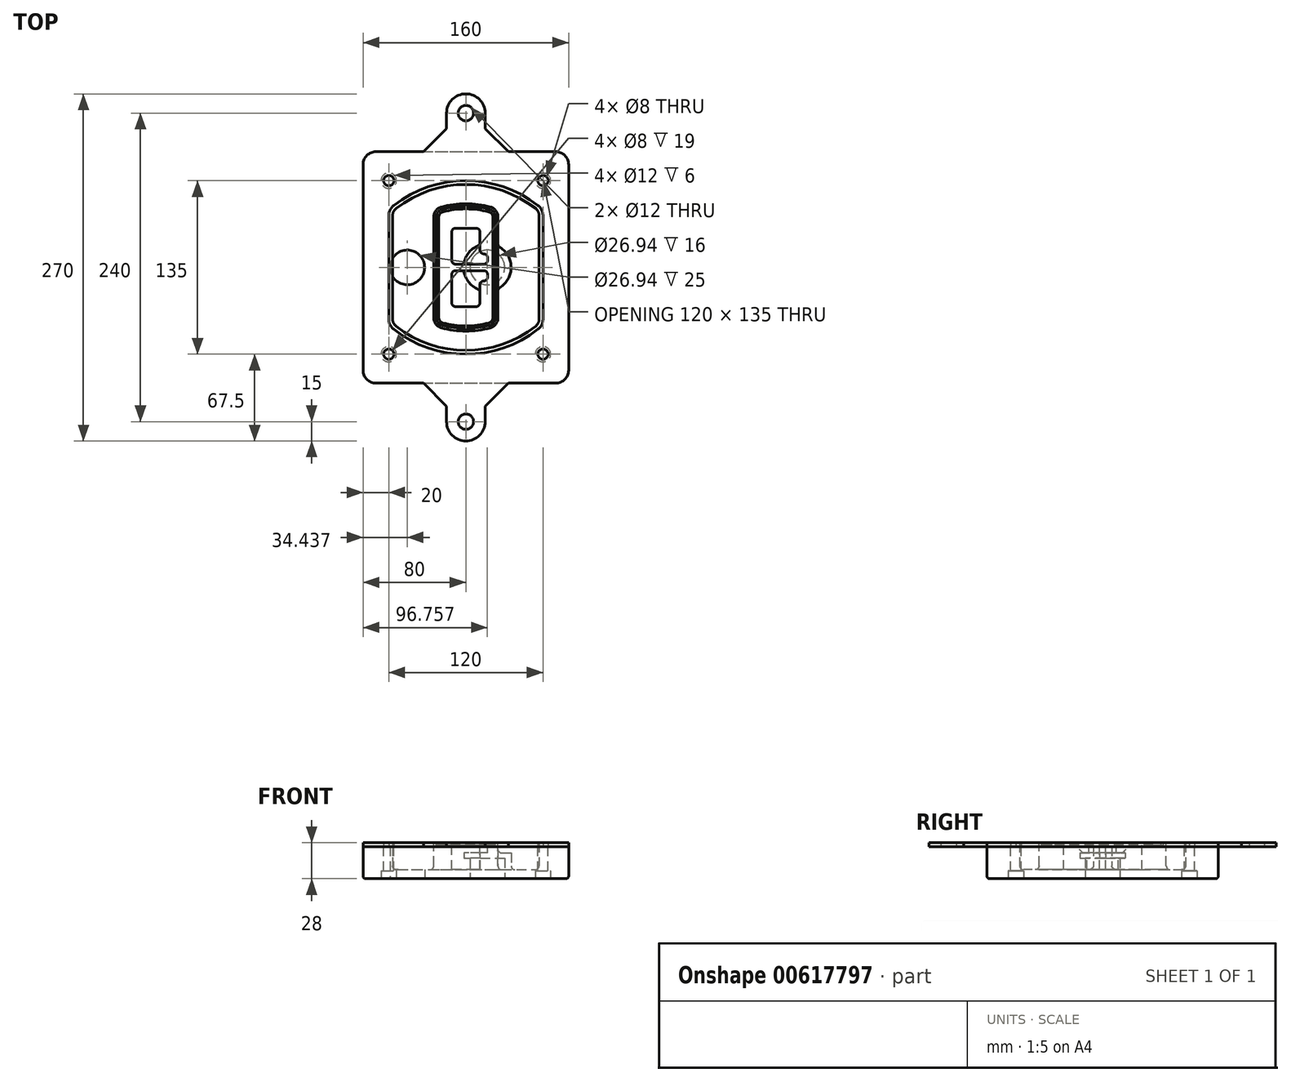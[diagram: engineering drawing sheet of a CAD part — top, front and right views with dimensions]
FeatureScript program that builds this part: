
annotation { "Feature Type Name" : "Feature", "Feature Type Description" : "" }
export const myFeature = defineFeature(function(context is Context, id is Id, definition is map)
    precondition{}
    {
        {
            var Q0;
            Q0=qCreatedBy(makeId("Top.planeOp"),FACE);
            var sketch = newSketch(context, id + "F0", { "sketchPlane" : qUnion([Q0])});
            skPoint(sketch, "E0.rect.middle", {"position": v(0, 0) * mm});
            skLineSegment(sketch, "E1.bottom", {"start": v(-70, -90) * mm, "end": v(70, -90) * mm});
            skLineSegment(sketch, "E1.top", {"start": v(-70, 90) * mm, "end": v(70, 90) * mm});
            skLineSegment(sketch, "E1.left", {"start": v(-80, -80) * mm, "end": v(-80, 80) * mm});
            skLineSegment(sketch, "E1.right", {"start": v(80, -80) * mm, "end": v(80, 80) * mm});
            skLineSegment(sketch, "E2", {"start": v(-80, 90) * mm, "end": v(80, -90) * mm, "construction": true});
            skLineSegment(sketch, "E3", {"start": v(80, 90) * mm, "end": v(-80, -90) * mm, "construction": true});
            skCircle(sketch, "E4", {"center": v(-60, 67.5) * mm, "radius": 4 * mm});
            skCircle(sketch, "E5", {"center": v(60, 67.5) * mm, "radius": 4 * mm});
            skCircle(sketch, "E6", {"center": v(60, -67.5) * mm, "radius": 4 * mm});
            skCircle(sketch, "E7", {"center": v(-60, -67.5) * mm, "radius": 4 * mm});
            skLineSegment(sketch, "E8", {"start": v(-60, 67.5) * mm, "end": v(60, 67.5) * mm, "construction": true});
            skLineSegment(sketch, "E9", {"start": v(60, 67.5) * mm, "end": v(60, -67.5) * mm, "construction": true});
            skLineSegment(sketch, "E10", {"start": v(60, -67.5) * mm, "end": v(-60, -67.5) * mm, "construction": true});
            skLineSegment(sketch, "E11", {"start": v(-60, -67.5) * mm, "end": v(-60, 67.5) * mm, "construction": true});
            skLineSegment(sketch, "E12", {"start": v(-60, 40.3) * mm, "end": v(-60, -40.3) * mm});
            skLineSegment(sketch, "E13", {"start": v(60, 40.3) * mm, "end": v(60, -40.3) * mm});
            skArc(sketch, "E14", {"start": v(56.15, 48.18) * mm, "mid": v(0, 67.5) * mm, "end": v(-56.15, 48.18) * mm});
            skArc(sketch, "E15", {"start": v(-56.15, -48.18) * mm, "mid": v(0, -67.5) * mm, "end": v(56.15, -48.18) * mm});
            skLineSegment(sketch, "E16", {"start": v(-60, 0) * mm, "end": v(60, 0) * mm, "construction": true});
            skPoint(sketch, "E17.visualSharp", {"position": v(-60, -45) * mm});
            skArc(sketch, "E17.filletArc", {"start": v(-60, -40.3) * mm, "mid": v(-58.99, -44.68) * mm, "end": v(-56.15, -48.18) * mm});
            skPoint(sketch, "E18.visualSharp", {"position": v(-60, 45) * mm});
            skArc(sketch, "E18.filletArc", {"start": v(-56.15, 48.18) * mm, "mid": v(-58.99, 44.68) * mm, "end": v(-60, 40.3) * mm});
            skPoint(sketch, "E19.visualSharp", {"position": v(60, 45) * mm});
            skArc(sketch, "E19.filletArc", {"start": v(60, 40.3) * mm, "mid": v(58.99, 44.68) * mm, "end": v(56.15, 48.18) * mm});
            skPoint(sketch, "E20.visualSharp", {"position": v(60, -45) * mm});
            skArc(sketch, "E20.filletArc", {"start": v(56.15, -48.18) * mm, "mid": v(58.99, -44.68) * mm, "end": v(60, -40.3) * mm});
            skPoint(sketch, "E21.visualSharp", {"position": v(-80, 90) * mm});
            skArc(sketch, "E21.filletArc", {"start": v(-70, 90) * mm, "mid": v(-77.07, 87.07) * mm, "end": v(-80, 80) * mm});
            skPoint(sketch, "E22.visualSharp", {"position": v(80, 90) * mm});
            skArc(sketch, "E22.filletArc", {"start": v(80, 80) * mm, "mid": v(77.07, 87.07) * mm, "end": v(70, 90) * mm});
            skPoint(sketch, "E23.visualSharp", {"position": v(80, -90) * mm});
            skArc(sketch, "E23.filletArc", {"start": v(70, -90) * mm, "mid": v(77.07, -87.07) * mm, "end": v(80, -80) * mm});
            skPoint(sketch, "E24.visualSharp", {"position": v(-80, -90) * mm});
            skArc(sketch, "E24.filletArc", {"start": v(-80, -80) * mm, "mid": v(-77.07, -87.07) * mm, "end": v(-70, -90) * mm});
            skArc(sketch, "E25.0", {"start": v(57, 40.3) * mm, "mid": v(56.3, 43.36) * mm, "end": v(54.3, 45.81) * mm});
            skLineSegment(sketch, "E25.1", {"start": v(57, 40.3) * mm, "end": v(57, -40.3) * mm});
            skArc(sketch, "E25.2", {"start": v(54.3, -45.81) * mm, "mid": v(56.3, -43.36) * mm, "end": v(57, -40.3) * mm});
            skArc(sketch, "E25.3", {"start": v(-54.3, -45.81) * mm, "mid": v(0, -64.5) * mm, "end": v(54.3, -45.81) * mm});
            skArc(sketch, "E25.4", {"start": v(-57, -40.3) * mm, "mid": v(-56.3, -43.36) * mm, "end": v(-54.3, -45.81) * mm});
            skArc(sketch, "E25.5", {"start": v(54.3, 45.81) * mm, "mid": v(0, 64.5) * mm, "end": v(-54.3, 45.81) * mm});
            skLineSegment(sketch, "E25.6", {"start": v(-57, 40.3) * mm, "end": v(-57, -40.3) * mm});
            skArc(sketch, "E25.7", {"start": v(-54.3, 45.81) * mm, "mid": v(-56.3, 43.36) * mm, "end": v(-57, 40.3) * mm});
            skArc(sketch, "E26.0", {"start": v(-58.62, 51.33) * mm, "mid": v(-62.58, 46.43) * mm, "end": v(-64, 40.3) * mm});
            skArc(sketch, "E26.1", {"start": v(58.62, 51.33) * mm, "mid": v(0, 71.5) * mm, "end": v(-58.62, 51.33) * mm});
            skArc(sketch, "E26.2", {"start": v(64, 40.3) * mm, "mid": v(62.58, 46.43) * mm, "end": v(58.62, 51.33) * mm});
            skLineSegment(sketch, "E26.3", {"start": v(64, 40.3) * mm, "end": v(64, -40.3) * mm});
            skArc(sketch, "E26.4", {"start": v(58.62, -51.33) * mm, "mid": v(62.58, -46.43) * mm, "end": v(64, -40.3) * mm});
            skLineSegment(sketch, "E26.5", {"start": v(-64, 40.3) * mm, "end": v(-64, -40.3) * mm});
            skArc(sketch, "E26.6", {"start": v(-58.62, -51.33) * mm, "mid": v(0, -71.5) * mm, "end": v(58.62, -51.33) * mm});
            skArc(sketch, "E26.7", {"start": v(-64, -40.3) * mm, "mid": v(-62.58, -46.43) * mm, "end": v(-58.62, -51.33) * mm});
            skSolve(sketch);
        }
        {
            var Q0;
            Q0=makeQuery(id+"F0.imprint","IMPRINT",FACE,{"disambiguationData":[TD([[makeQuery(id+"F0.imprint","IMPRINT",EDGE,{"derivedFrom":sQuery(id+"F0.wireOp",EDGE,"E1.bottom")}),1.0]])]});
            var Q1;
            Q1=makeQuery(id+"F0.imprint","IMPRINT",FACE,{"disambiguationData":[TD([[makeQuery(id+"F0.imprint","IMPRINT",EDGE,{"derivedFrom":sQuery(id+"F0.wireOp",EDGE,"E12")}),1.0]])]});
            var Q2;
            Q2=makeQuery(id+"F0.imprint","IMPRINT",FACE,{"disambiguationData":[TD([[makeQuery(id+"F0.imprint","IMPRINT",EDGE,{"derivedFrom":sQuery(id+"F0.wireOp",EDGE,"E25.0")}),1.0]])]});
            var Q3;
            Q3=makeQuery(id+"F0.imprint","IMPRINT",FACE,{"disambiguationData":[TD([[makeQuery(id+"F0.imprint","IMPRINT",EDGE,{"derivedFrom":sQuery(id+"F0.wireOp",EDGE,"E12")}),-1.0]])]});
            extrude(context, id + "F1", {"entities" : qUnion([Q0, Q1, Q2, Q3]), "oppositeDirection" : true, "depth" : 25 * mm});
        }
        {
            var Q0;
            Q0=makeQuery(id+"F0.imprint","IMPRINT",FACE,{"disambiguationData":[TD([[makeQuery(id+"F0.imprint","IMPRINT",EDGE,{"derivedFrom":sQuery(id+"F0.wireOp",EDGE,"E12")}),1.0]])]});
            extrude(context, id + "F2", {"entities" : qUnion([Q0]), "operationType" : NewBodyOperationType.ADD, "depth" : 3 * mm});
        }
        {
            var Q0;
            Q0=makeQuery(id+"F0.imprint","IMPRINT",FACE,{"disambiguationData":[TD([[makeQuery(id+"F0.imprint","IMPRINT",EDGE,{"derivedFrom":sQuery(id+"F0.wireOp",EDGE,"E25.0")}),1.0]])]});
            extrude(context, id + "F3", {"entities" : qUnion([Q0]), "operationType" : NewBodyOperationType.REMOVE, "oppositeDirection" : true, "depth" : 18 * mm});
        }
        {
            var Q0;
            Q0=makeQuery(id+"F2.opExtrude","CAP_FACE",FACE,{"disambiguationData":[OSD([sQuery(id+"F0.wireOp",EDGE,"E12"),sQuery(id+"F0.wireOp",EDGE,"E13"),sQuery(id+"F0.wireOp",EDGE,"E14"),sQuery(id+"F0.wireOp",EDGE,"E15"),sQuery(id+"F0.wireOp",EDGE,"E17.filletArc"),sQuery(id+"F0.wireOp",EDGE,"E18.filletArc"),sQuery(id+"F0.wireOp",EDGE,"E19.filletArc"),sQuery(id+"F0.wireOp",EDGE,"E20.filletArc"),sQuery(id+"F0.wireOp",EDGE,"E25.0"),sQuery(id+"F0.wireOp",EDGE,"E25.1"),sQuery(id+"F0.wireOp",EDGE,"E25.2"),sQuery(id+"F0.wireOp",EDGE,"E25.3"),sQuery(id+"F0.wireOp",EDGE,"E25.4"),sQuery(id+"F0.wireOp",EDGE,"E25.5"),sQuery(id+"F0.wireOp",EDGE,"E25.6"),sQuery(id+"F0.wireOp",EDGE,"E25.7")])],"isStart":false});
            var sketch = newSketch(context, id + "F4", { "sketchPlane" : qUnion([Q0])});
            skArc(sketch, "E27.0", {"start": v(-19.08, -46.97) * mm, "mid": v(0, -49.5) * mm, "end": v(19.08, -46.97) * mm});
            skArc(sketch, "E28.0", {"start": v(19.08, 46.97) * mm, "mid": v(0, 49.5) * mm, "end": v(-19.08, 46.97) * mm});
            skLineSegment(sketch, "E29", {"start": v(-25, 39.25) * mm, "end": v(-25, -39.25) * mm});
            skLineSegment(sketch, "E30", {"start": v(25, 39.25) * mm, "end": v(25, -39.25) * mm});
            skLineSegment(sketch, "E31", {"start": v(-25, 45.1) * mm, "end": v(25, 45.1) * mm, "construction": true});
            skLineSegment(sketch, "E32", {"start": v(-25, -45.1) * mm, "end": v(25, -45.1) * mm, "construction": true});
            skPoint(sketch, "E33.visualSharp", {"position": v(-25, 45.1) * mm});
            skArc(sketch, "E33.filletArc", {"start": v(-19.08, 46.97) * mm, "mid": v(-23.35, 44.11) * mm, "end": v(-25, 39.25) * mm});
            skPoint(sketch, "E34.visualSharp", {"position": v(25, 45.1) * mm});
            skArc(sketch, "E34.filletArc", {"start": v(25, 39.25) * mm, "mid": v(23.35, 44.11) * mm, "end": v(19.08, 46.97) * mm});
            skPoint(sketch, "E35.visualSharp", {"position": v(25, -45.1) * mm});
            skArc(sketch, "E35.filletArc", {"start": v(19.08, -46.97) * mm, "mid": v(23.35, -44.11) * mm, "end": v(25, -39.25) * mm});
            skPoint(sketch, "E36.visualSharp", {"position": v(-25, -45.1) * mm});
            skArc(sketch, "E36.filletArc", {"start": v(-25, -39.25) * mm, "mid": v(-23.35, -44.11) * mm, "end": v(-19.08, -46.97) * mm});
            skArc(sketch, "E37.0", {"start": v(54.3, 45.81) * mm, "mid": v(0, 64.5) * mm, "end": v(-54.3, 45.81) * mm});
            skArc(sketch, "E37.1", {"start": v(-54.3, 45.81) * mm, "mid": v(-56.3, 43.36) * mm, "end": v(-57, 40.3) * mm});
            skLineSegment(sketch, "E37.2", {"start": v(-57, 40.3) * mm, "end": v(-57, -40.3) * mm});
            skArc(sketch, "E37.3", {"start": v(-57, -40.3) * mm, "mid": v(-56.3, -43.36) * mm, "end": v(-54.3, -45.81) * mm});
            skArc(sketch, "E37.4", {"start": v(-54.3, -45.81) * mm, "mid": v(0, -64.5) * mm, "end": v(54.3, -45.81) * mm});
            skArc(sketch, "E37.5", {"start": v(54.3, -45.81) * mm, "mid": v(56.3, -43.36) * mm, "end": v(57, -40.3) * mm});
            skLineSegment(sketch, "E37.6", {"start": v(57, 40.3) * mm, "end": v(57, -40.3) * mm});
            skArc(sketch, "E37.7", {"start": v(57, 40.3) * mm, "mid": v(56.3, 43.36) * mm, "end": v(54.3, 45.81) * mm});
            skLineSegment(sketch, "E38.0", {"start": v(23, 39.25) * mm, "end": v(23, -39.25) * mm});
            skArc(sketch, "E38.1", {"start": v(18.56, -45.04) * mm, "mid": v(21.76, -42.9) * mm, "end": v(23, -39.25) * mm});
            skArc(sketch, "E38.2", {"start": v(-18.56, -45.04) * mm, "mid": v(0, -47.5) * mm, "end": v(18.56, -45.04) * mm});
            skArc(sketch, "E38.3", {"start": v(-23, -39.25) * mm, "mid": v(-21.76, -42.9) * mm, "end": v(-18.56, -45.04) * mm});
            skLineSegment(sketch, "E38.4", {"start": v(-23, 39.25) * mm, "end": v(-23, -39.25) * mm});
            skArc(sketch, "E38.5", {"start": v(23, 39.25) * mm, "mid": v(21.76, 42.9) * mm, "end": v(18.56, 45.04) * mm});
            skArc(sketch, "E38.6", {"start": v(-18.56, 45.04) * mm, "mid": v(-21.76, 42.9) * mm, "end": v(-23, 39.25) * mm});
            skArc(sketch, "E38.7", {"start": v(18.56, 45.04) * mm, "mid": v(0, 47.5) * mm, "end": v(-18.56, 45.04) * mm});
            skArc(sketch, "E39.0", {"start": v(21, 39.25) * mm, "mid": v(20.18, 41.68) * mm, "end": v(18.04, 43.1) * mm});
            skLineSegment(sketch, "E39.1", {"start": v(21, 39.25) * mm, "end": v(21, -39.25) * mm});
            skArc(sketch, "E39.2", {"start": v(18.04, -43.1) * mm, "mid": v(20.18, -41.68) * mm, "end": v(21, -39.25) * mm});
            skArc(sketch, "E39.3", {"start": v(-18.04, -43.1) * mm, "mid": v(0, -45.5) * mm, "end": v(18.04, -43.1) * mm});
            skArc(sketch, "E39.4", {"start": v(-21, -39.25) * mm, "mid": v(-20.18, -41.68) * mm, "end": v(-18.04, -43.1) * mm});
            skArc(sketch, "E39.5", {"start": v(18.04, 43.1) * mm, "mid": v(0, 45.5) * mm, "end": v(-18.04, 43.1) * mm});
            skLineSegment(sketch, "E39.6", {"start": v(-21, 39.25) * mm, "end": v(-21, -39.25) * mm});
            skArc(sketch, "E39.7", {"start": v(-18.04, 43.1) * mm, "mid": v(-20.18, 41.68) * mm, "end": v(-21, 39.25) * mm});
            skLineSegment(sketch, "E40", {"start": v(-25, 0) * mm, "end": v(25, 0) * mm, "construction": true});
            skLineSegment(sketch, "E41", {"start": v(-11, 5.5) * mm, "end": v(-11, 27.5) * mm});
            skLineSegment(sketch, "E42", {"start": v(-8, 30.5) * mm, "end": v(8, 30.5) * mm});
            skLineSegment(sketch, "E43", {"start": v(11, 27.5) * mm, "end": v(11, 13.5) * mm});
            skLineSegment(sketch, "E44", {"start": v(14, 10.5) * mm, "end": v(14, 10.5) * mm});
            skLineSegment(sketch, "E45", {"start": v(17, 7.5) * mm, "end": v(17, 5.5) * mm});
            skLineSegment(sketch, "E46", {"start": v(14, 2.5) * mm, "end": v(-8, 2.5) * mm});
            skPoint(sketch, "E47.visualSharp", {"position": v(-11, 30.5) * mm});
            skArc(sketch, "E47.filletArc", {"start": v(-8, 30.5) * mm, "mid": v(-10.12, 29.62) * mm, "end": v(-11, 27.5) * mm});
            skPoint(sketch, "E48.visualSharp", {"position": v(11, 30.5) * mm});
            skArc(sketch, "E48.filletArc", {"start": v(11, 27.5) * mm, "mid": v(10.12, 29.62) * mm, "end": v(8, 30.5) * mm});
            skPoint(sketch, "E49.visualSharp", {"position": v(11, 10.5) * mm});
            skArc(sketch, "E49.filletArc", {"start": v(11, 13.5) * mm, "mid": v(11.88, 11.38) * mm, "end": v(14, 10.5) * mm});
            skPoint(sketch, "E50.visualSharp", {"position": v(17, 10.5) * mm});
            skArc(sketch, "E50.filletArc", {"start": v(17, 7.5) * mm, "mid": v(16.12, 9.62) * mm, "end": v(14, 10.5) * mm});
            skPoint(sketch, "E51.visualSharp", {"position": v(17, 2.5) * mm});
            skArc(sketch, "E51.filletArc", {"start": v(14, 2.5) * mm, "mid": v(16.12, 3.38) * mm, "end": v(17, 5.5) * mm});
            skPoint(sketch, "E52.visualSharp", {"position": v(-11, 2.5) * mm});
            skArc(sketch, "E52.filletArc", {"start": v(-11, 5.5) * mm, "mid": v(-10.12, 3.38) * mm, "end": v(-8, 2.5) * mm});
            skLineSegment(sketch, "E53.0.MirrorCS", {"start": v(14, -2.5) * mm, "end": v(-8, -2.5) * mm});
            skArc(sketch, "E54.0.MirrorCS", {"start": v(-11, -5.5) * mm, "mid": v(-10.12, -3.38) * mm, "end": v(-8, -2.5) * mm});
            skLineSegment(sketch, "E55.0.MirrorCS", {"start": v(-11, -5.5) * mm, "end": v(-11, -27.5) * mm});
            skArc(sketch, "E56.0.MirrorCS", {"start": v(-8, -30.5) * mm, "mid": v(-10.12, -29.62) * mm, "end": v(-11, -27.5) * mm});
            skLineSegment(sketch, "E57.0.MirrorCS", {"start": v(-8, -30.5) * mm, "end": v(8, -30.5) * mm});
            skArc(sketch, "E58.0.MirrorCS", {"start": v(11, -27.5) * mm, "mid": v(10.12, -29.62) * mm, "end": v(8, -30.5) * mm});
            skLineSegment(sketch, "E59.0.MirrorCS", {"start": v(11, -27.5) * mm, "end": v(11, -13.5) * mm});
            skArc(sketch, "E60.0.MirrorCS", {"start": v(11, -13.5) * mm, "mid": v(11.88, -11.38) * mm, "end": v(14, -10.5) * mm});
            skArc(sketch, "E61.0.MirrorCS", {"start": v(17, -7.5) * mm, "mid": v(16.12, -9.62) * mm, "end": v(14, -10.5) * mm});
            skLineSegment(sketch, "E62.0.MirrorCS", {"start": v(17, -7.5) * mm, "end": v(17, -5.5) * mm});
            skArc(sketch, "E63.0.MirrorCS", {"start": v(14, -2.5) * mm, "mid": v(16.12, -3.38) * mm, "end": v(17, -5.5) * mm});
            skSolve(sketch);
        }
        {
            var Q0;
            Q0=makeQuery(id+"F4.imprint","IMPRINT",FACE,{"disambiguationData":[TD([[makeQuery(id+"F4.imprint","IMPRINT",EDGE,{"derivedFrom":sQuery(id+"F4.wireOp",EDGE,"E27.0")}),1.0]])]});
            var Q1;
            Q1=makeQuery(id+"F4.imprint","IMPRINT",FACE,{"disambiguationData":[TD([[makeQuery(id+"F4.imprint","IMPRINT",EDGE,{"derivedFrom":sQuery(id+"F4.wireOp",EDGE,"E38.0")}),-1.0]])]});
            var Q2;
            Q2=makeQuery(id+"F4.imprint","IMPRINT",FACE,{"disambiguationData":[TD([[makeQuery(id+"F4.imprint","IMPRINT",EDGE,{"derivedFrom":sQuery(id+"F4.wireOp",EDGE,"E39.0")}),1.0]])]});
            extrude(context, id + "F5", {"entities" : qUnion([Q0, Q1, Q2]), "operationType" : NewBodyOperationType.ADD, "endBound" : BoundingType.UP_TO_NEXT, "oppositeDirection" : true, "depth" : 25 * mm});
        }
        {
            var Q0;
            Q0=makeQuery(id+"F4.imprint","IMPRINT",FACE,{"disambiguationData":[TD([[makeQuery(id+"F4.imprint","IMPRINT",EDGE,{"derivedFrom":sQuery(id+"F4.wireOp",EDGE,"E38.0")}),-1.0]])]});
            extrude(context, id + "F6", {"entities" : qUnion([Q0]), "operationType" : NewBodyOperationType.REMOVE, "oppositeDirection" : true, "depth" : 2 * mm});
        }
        {
            var Q0;
            Q0=makeQuery(id+"F1.opExtrude","CAP_FACE",FACE,{"disambiguationData":[OSD([sQuery(id+"F0.wireOp",EDGE,"E1.bottom"),sQuery(id+"F0.wireOp",EDGE,"E1.top"),sQuery(id+"F0.wireOp",EDGE,"E1.left"),sQuery(id+"F0.wireOp",EDGE,"E1.right"),sQuery(id+"F0.wireOp",EDGE,"E4"),sQuery(id+"F0.wireOp",EDGE,"E5"),sQuery(id+"F0.wireOp",EDGE,"E6"),sQuery(id+"F0.wireOp",EDGE,"E7"),sQuery(id+"F0.wireOp",EDGE,"E21.filletArc"),sQuery(id+"F0.wireOp",EDGE,"E22.filletArc"),sQuery(id+"F0.wireOp",EDGE,"E23.filletArc"),sQuery(id+"F0.wireOp",EDGE,"E24.filletArc")])],"isStart":false});
            var sketch = newSketch(context, id + "F7", { "sketchPlane" : qUnion([Q0])});
            skCircle(sketch, "E64", {"center": v(16.76, 0) * mm, "radius": 13.47 * mm});
            skCircle(sketch, "E65", {"center": v(-45.56, 0) * mm, "radius": 13.47 * mm});
            skLineSegment(sketch, "E66", {"start": v(80, 0) * mm, "end": v(-80, 0) * mm});
            skCircle(sketch, "E67", {"center": v(16.76, 0) * mm, "radius": 18.47 * mm});
            skCircle(sketch, "E68", {"center": v(60, -67.5) * mm, "radius": 6 * mm});
            skCircle(sketch, "E69", {"center": v(-60, -67.5) * mm, "radius": 6 * mm});
            skCircle(sketch, "E70", {"center": v(-60, 67.5) * mm, "radius": 6 * mm});
            skCircle(sketch, "E71", {"center": v(60, 67.5) * mm, "radius": 6 * mm});
            skSolve(sketch);
        }
        {
            var Q0;
            {var subQ1=sQuery(id+"F7.wireOp",EDGE,"E66");var subQ4=sQuery(id+"F7.wireOp",EDGE,"E64");var subQ6=makeQuery(id+"F7.imprint","INTERSECT",VERTEX,{"disambiguationData":[OD(0.0)],"derivedFrom":[subQ4,subQ1]});Q0=makeQuery(id+"F7.imprint","IMPRINT",FACE,{"disambiguationData":[TD([[makeQuery(id+"F7.imprint","IMPRINT",EDGE,{"disambiguationData":[TD([[subQ6,-1.0]])],"derivedFrom":subQ4}),-1.0]])]});}
            var Q1;
            {var subQ0=sQuery(id+"F7.wireOp",EDGE,"E66");var subQ1=sQuery(id+"F7.wireOp",EDGE,"E64");var subQ3=makeQuery(id+"F7.imprint","INTERSECT",VERTEX,{"disambiguationData":[OD(0.0)],"derivedFrom":[subQ1,subQ0]});Q1=makeQuery(id+"F7.imprint","IMPRINT",FACE,{"disambiguationData":[TD([[makeQuery(id+"F7.imprint","IMPRINT",EDGE,{"disambiguationData":[TD([[subQ3,-1.0]])],"derivedFrom":subQ1}),1.0]])]});}
            var Q2;
            {var subQ0=sQuery(id+"F7.wireOp",EDGE,"E66");var subQ1=sQuery(id+"F7.wireOp",EDGE,"E64");var subQ3=makeQuery(id+"F7.imprint","INTERSECT",VERTEX,{"disambiguationData":[OD(0.0)],"derivedFrom":[subQ1,subQ0]});Q2=makeQuery(id+"F7.imprint","IMPRINT",FACE,{"disambiguationData":[TD([[makeQuery(id+"F7.imprint","IMPRINT",EDGE,{"disambiguationData":[TD([[subQ3,1.0]])],"derivedFrom":subQ1}),1.0]])]});}
            var Q3;
            {var subQ1=sQuery(id+"F7.wireOp",EDGE,"E66");var subQ4=sQuery(id+"F7.wireOp",EDGE,"E64");var subQ6=makeQuery(id+"F7.imprint","INTERSECT",VERTEX,{"disambiguationData":[OD(0.0)],"derivedFrom":[subQ4,subQ1]});Q3=makeQuery(id+"F7.imprint","IMPRINT",FACE,{"disambiguationData":[TD([[makeQuery(id+"F7.imprint","IMPRINT",EDGE,{"disambiguationData":[TD([[subQ6,1.0]])],"derivedFrom":subQ4}),-1.0]])]});}
            extrude(context, id + "F8", {"entities" : qUnion([Q0, Q1, Q2, Q3]), "operationType" : NewBodyOperationType.ADD, "oppositeDirection" : true, "depth" : 20 * mm});
        }
        {
            var Q0;
            {var subQ0=sQuery(id+"F7.wireOp",EDGE,"E66");var subQ1=sQuery(id+"F7.wireOp",EDGE,"E64");var subQ3=makeQuery(id+"F7.imprint","INTERSECT",VERTEX,{"disambiguationData":[OD(0.0)],"derivedFrom":[subQ1,subQ0]});Q0=makeQuery(id+"F7.imprint","IMPRINT",FACE,{"disambiguationData":[TD([[makeQuery(id+"F7.imprint","IMPRINT",EDGE,{"disambiguationData":[TD([[subQ3,-1.0]])],"derivedFrom":subQ1}),1.0]])]});}
            var Q1;
            {var subQ0=sQuery(id+"F7.wireOp",EDGE,"E66");var subQ1=sQuery(id+"F7.wireOp",EDGE,"E64");var subQ3=makeQuery(id+"F7.imprint","INTERSECT",VERTEX,{"disambiguationData":[OD(0.0)],"derivedFrom":[subQ1,subQ0]});Q1=makeQuery(id+"F7.imprint","IMPRINT",FACE,{"disambiguationData":[TD([[makeQuery(id+"F7.imprint","IMPRINT",EDGE,{"disambiguationData":[TD([[subQ3,1.0]])],"derivedFrom":subQ1}),1.0]])]});}
            extrude(context, id + "F9", {"entities" : qUnion([Q0, Q1]), "operationType" : NewBodyOperationType.REMOVE, "oppositeDirection" : true, "depth" : 16 * mm});
        }
        {
            var Q0;
            {var subQ0=sQuery(id+"F7.wireOp",EDGE,"E66");var subQ1=sQuery(id+"F7.wireOp",EDGE,"E65");var subQ3=makeQuery(id+"F7.imprint","INTERSECT",VERTEX,{"disambiguationData":[OD(0.0)],"derivedFrom":[subQ1,subQ0]});Q0=makeQuery(id+"F7.imprint","IMPRINT",FACE,{"disambiguationData":[TD([[makeQuery(id+"F7.imprint","IMPRINT",EDGE,{"disambiguationData":[TD([[subQ3,-1.0]])],"derivedFrom":subQ1}),1.0]])]});}
            var Q1;
            {var subQ0=sQuery(id+"F7.wireOp",EDGE,"E66");var subQ1=sQuery(id+"F7.wireOp",EDGE,"E65");var subQ3=makeQuery(id+"F7.imprint","INTERSECT",VERTEX,{"disambiguationData":[OD(0.0)],"derivedFrom":[subQ1,subQ0]});Q1=makeQuery(id+"F7.imprint","IMPRINT",FACE,{"disambiguationData":[TD([[makeQuery(id+"F7.imprint","IMPRINT",EDGE,{"disambiguationData":[TD([[subQ3,1.0]])],"derivedFrom":subQ1}),1.0]])]});}
            extrude(context, id + "F10", {"entities" : qUnion([Q0, Q1]), "operationType" : NewBodyOperationType.REMOVE, "oppositeDirection" : true, "depth" : 25 * mm});
        }
        {
            var Q0;
            Q0=makeQuery(id+"F7.imprint","IMPRINT",FACE,{"disambiguationData":[TD([[makeQuery(id+"F7.imprint","IMPRINT",EDGE,{"derivedFrom":sQuery(id+"F7.wireOp",EDGE,"E68")}),1.0]])]});
            var Q1;
            Q1=makeQuery(id+"F7.imprint","IMPRINT",FACE,{"disambiguationData":[TD([[makeQuery(id+"F7.imprint","IMPRINT",EDGE,{"derivedFrom":makeQuery(id+"F1.opExtrude","CAP_EDGE",EDGE,{"disambiguationData":[OSD([sQuery(id+"F0.wireOp",EDGE,"E5")])],"isStart":false})}),-1.0]])]});
            var Q2;
            Q2=makeQuery(id+"F7.imprint","IMPRINT",FACE,{"disambiguationData":[TD([[makeQuery(id+"F7.imprint","IMPRINT",EDGE,{"derivedFrom":sQuery(id+"F7.wireOp",EDGE,"E69")}),1.0]])]});
            var Q3;
            Q3=makeQuery(id+"F7.imprint","IMPRINT",FACE,{"disambiguationData":[TD([[makeQuery(id+"F7.imprint","IMPRINT",EDGE,{"derivedFrom":makeQuery(id+"F1.opExtrude","CAP_EDGE",EDGE,{"disambiguationData":[OSD([sQuery(id+"F0.wireOp",EDGE,"E4")])],"isStart":false})}),-1.0]])]});
            var Q4;
            Q4=makeQuery(id+"F7.imprint","IMPRINT",FACE,{"disambiguationData":[TD([[makeQuery(id+"F7.imprint","IMPRINT",EDGE,{"derivedFrom":sQuery(id+"F7.wireOp",EDGE,"E70")}),1.0]])]});
            var Q5;
            Q5=makeQuery(id+"F7.imprint","IMPRINT",FACE,{"disambiguationData":[TD([[makeQuery(id+"F7.imprint","IMPRINT",EDGE,{"derivedFrom":makeQuery(id+"F1.opExtrude","CAP_EDGE",EDGE,{"disambiguationData":[OSD([sQuery(id+"F0.wireOp",EDGE,"E7")])],"isStart":false})}),-1.0]])]});
            var Q6;
            Q6=makeQuery(id+"F7.imprint","IMPRINT",FACE,{"disambiguationData":[TD([[makeQuery(id+"F7.imprint","IMPRINT",EDGE,{"derivedFrom":sQuery(id+"F7.wireOp",EDGE,"E71")}),1.0]])]});
            var Q7;
            Q7=makeQuery(id+"F7.imprint","IMPRINT",FACE,{"disambiguationData":[TD([[makeQuery(id+"F7.imprint","IMPRINT",EDGE,{"derivedFrom":makeQuery(id+"F1.opExtrude","CAP_EDGE",EDGE,{"disambiguationData":[OSD([sQuery(id+"F0.wireOp",EDGE,"E6")])],"isStart":false})}),-1.0]])]});
            extrude(context, id + "F11", {"entities" : qUnion([Q0, Q1, Q2, Q3, Q4, Q5, Q6, Q7]), "operationType" : NewBodyOperationType.REMOVE, "oppositeDirection" : true, "depth" : 6 * mm});
        }
        {
            var Q0;
            Q0=makeQuery(id+"F9.boolean.opBoolean","COPY",FACE,{"derivedFrom":makeQuery(id+"F9.opExtrude","CAP_FACE",FACE,{"disambiguationData":[OSD([sQuery(id+"F7.wireOp",EDGE,"E64")])],"isStart":false})});
            var sketch = newSketch(context, id + "F12", { "sketchPlane" : qUnion([Q0])});
            skArc(sketch, "E72.0", {"start": v(11, 17.55) * mm, "mid": v(2.57, 11.82) * mm, "end": v(-1.54, 2.5) * mm});
            skArc(sketch, "E72.1", {"start": v(-1.54, -2.5) * mm, "mid": v(2.57, -11.82) * mm, "end": v(11, -17.55) * mm});
            skLineSegment(sketch, "E73", {"start": v(-1.54, -2.5) * mm, "end": v(14, -2.5) * mm});
            skLineSegment(sketch, "E74.0", {"start": v(14, 2.5) * mm, "end": v(-1.54, 2.5) * mm});
            skArc(sketch, "E74.1", {"start": v(14, 2.5) * mm, "mid": v(16.12, 3.38) * mm, "end": v(17, 5.5) * mm});
            skLineSegment(sketch, "E74.2", {"start": v(17, 7.5) * mm, "end": v(17, 5.5) * mm});
            skArc(sketch, "E74.3", {"start": v(17, 7.5) * mm, "mid": v(16.12, 9.62) * mm, "end": v(14, 10.5) * mm});
            skArc(sketch, "E74.4", {"start": v(11, 13.5) * mm, "mid": v(11.88, 11.38) * mm, "end": v(14, 10.5) * mm});
            skLineSegment(sketch, "E74.5", {"start": v(11, 17.55) * mm, "end": v(11, 13.5) * mm});
            skLineSegment(sketch, "E74.7", {"start": v(14, -2.5) * mm, "end": v(-1.54, -2.5) * mm});
            skArc(sketch, "E74.8", {"start": v(14, -2.5) * mm, "mid": v(16.12, -3.38) * mm, "end": v(17, -5.5) * mm});
            skLineSegment(sketch, "E74.9", {"start": v(17, -7.5) * mm, "end": v(17, -5.5) * mm});
            skArc(sketch, "E74.10", {"start": v(17, -7.5) * mm, "mid": v(16.12, -9.62) * mm, "end": v(14, -10.5) * mm});
            skArc(sketch, "E74.11", {"start": v(11, -13.5) * mm, "mid": v(11.88, -11.38) * mm, "end": v(14, -10.5) * mm});
            skLineSegment(sketch, "E74.12", {"start": v(11, -17.55) * mm, "end": v(11, -13.5) * mm});
            skPoint(sketch, "E75.orphan", {"position": v(11, -27.5) * mm});
            skPoint(sketch, "E76.orphan", {"position": v(-8, -2.5) * mm});
            skPoint(sketch, "E77.orphan", {"position": v(-8, 2.5) * mm});
            skPoint(sketch, "E78.orphan", {"position": v(11, 27.5) * mm});
            skSolve(sketch);
        }
        {
            var Q0;
            {var subQ7=sQuery(id+"F12.wireOp",EDGE,"E72.0");var subQ14=sQuery(id+"F12.wireOp",EDGE,"E72.1");var subQ16=sQuery(id+"F12.wireOp",EDGE,"E74.1");var subQ18=sQuery(id+"F12.wireOp",EDGE,"E74.8");Q0=qUnion([makeQuery(id+"F12.imprint","IMPRINT",FACE,{"disambiguationData":[TD([[makeQuery(id+"F12.imprint","IMPRINT",EDGE,{"derivedFrom":subQ7}),1.0]])]}),makeQuery(id+"F12.imprint","IMPRINT",FACE,{"disambiguationData":[TD([[makeQuery(id+"F12.imprint","IMPRINT",EDGE,{"derivedFrom":subQ14}),1.0]])]}),makeQuery(id+"F12.imprint","IMPRINT",FACE,{"disambiguationData":[TD([[makeQuery(id+"F12.imprint","IMPRINT",EDGE,{"derivedFrom":subQ16}),1.0]])]}),makeQuery(id+"F12.imprint","IMPRINT",FACE,{"disambiguationData":[TD([[makeQuery(id+"F12.imprint","IMPRINT",EDGE,{"derivedFrom":subQ18}),-1.0]])]})]);}
            var Q1;
            Q1=makeQuery(id+"F5.boolean.opBoolean","SPLIT",FACE,{"disambiguationData":[TD([makeQuery(id+"F5.opExtrude","SWEPT_FACE",FACE,{"disambiguationData":[OSD([sQuery(id+"F4.wireOp",EDGE,"E41")])]})])],"derivedFrom":makeQuery(id+"F3.boolean.opBoolean","COPY",FACE,{"derivedFrom":makeQuery(id+"F3.opExtrude","CAP_FACE",FACE,{"disambiguationData":[OSD([sQuery(id+"F0.wireOp",EDGE,"E25.0"),sQuery(id+"F0.wireOp",EDGE,"E25.1"),sQuery(id+"F0.wireOp",EDGE,"E25.2"),sQuery(id+"F0.wireOp",EDGE,"E25.3"),sQuery(id+"F0.wireOp",EDGE,"E25.4"),sQuery(id+"F0.wireOp",EDGE,"E25.5"),sQuery(id+"F0.wireOp",EDGE,"E25.6"),sQuery(id+"F0.wireOp",EDGE,"E25.7")])],"isStart":false})})});
            extrude(context, id + "F13", {"entities" : qUnion([Q0]), "operationType" : NewBodyOperationType.REMOVE, "endBound" : BoundingType.UP_TO_SURFACE, "endBoundEntityFace" : qUnion([Q1]), "depth" : 25 * mm});
        }
        {
            var Q0;
            Q0=makeQuery(id+"F3.boolean.opBoolean","COPY",EDGE,{"derivedFrom":makeQuery(id+"F3.opExtrude","CAP_EDGE",EDGE,{"disambiguationData":[OSD([sQuery(id+"F0.wireOp",EDGE,"E25.6")])],"isStart":false})});
            var Q1;
            Q1=makeQuery(id+"F8.boolean.opBoolean","INTERSECT",EDGE,{"derivedFrom":[makeQuery(id+"F5.opExtrude","SWEPT_FACE",FACE,{"disambiguationData":[OSD([sQuery(id+"F4.wireOp",EDGE,"E30")])]}),makeQuery(id+"F8.opExtrude","CAP_FACE",FACE,{"disambiguationData":[OSD([sQuery(id+"F7.wireOp",EDGE,"E67")])],"isStart":false})]});
            var Q2;
            Q2=makeQuery(id+"F8.boolean.opBoolean","INTERSECT",EDGE,{"disambiguationData":[OD(1.0)],"derivedFrom":[makeQuery(id+"F5.opExtrude","SWEPT_FACE",FACE,{"disambiguationData":[OSD([sQuery(id+"F4.wireOp",EDGE,"E30")])]}),makeQuery(id+"F8.opExtrude","SWEPT_FACE",FACE,{"disambiguationData":[OSD([sQuery(id+"F7.wireOp",EDGE,"E67")])]})]});
            var Q3;
            {var subQ0=sQuery(id+"F4.wireOp",EDGE,"E30");Q3=makeQuery(id+"F8.boolean.opBoolean","SPLIT",EDGE,{"disambiguationData":[TD([makeQuery(id+"F5.opExtrude","SWEPT_FACE",FACE,{"disambiguationData":[OSD([sQuery(id+"F4.wireOp",EDGE,"E35.filletArc")])]})])],"derivedFrom":makeQuery(id+"F5.opExtrude","CAP_EDGE",EDGE,{"disambiguationData":[OSD([subQ0])],"isStart":false})});}
            var Q4;
            {var subQ0=sQuery(id+"F0.wireOp",EDGE,"E25.7");var subQ1=sQuery(id+"F0.wireOp",EDGE,"E25.1");var subQ2=sQuery(id+"F0.wireOp",EDGE,"E25.6");var subQ3=sQuery(id+"F0.wireOp",EDGE,"E25.5");var subQ4=sQuery(id+"F0.wireOp",EDGE,"E25.4");var subQ5=sQuery(id+"F0.wireOp",EDGE,"E25.0");var subQ6=sQuery(id+"F0.wireOp",EDGE,"E25.2");var subQ7=sQuery(id+"F0.wireOp",EDGE,"E25.3");Q4=makeQuery(id+"F8.boolean.opBoolean","INTERSECT",EDGE,{"derivedFrom":[makeQuery(id+"F5.boolean.opBoolean","SPLIT",FACE,{"disambiguationData":[TD([makeQuery(id+"F2.opExtrude","SWEPT_FACE",FACE,{"disambiguationData":[OSD([subQ5])]})])],"derivedFrom":makeQuery(id+"F3.boolean.opBoolean","COPY",FACE,{"derivedFrom":makeQuery(id+"F3.opExtrude","CAP_FACE",FACE,{"disambiguationData":[OSD([subQ5,subQ1,subQ6,subQ7,subQ4,subQ3,subQ2,subQ0])],"isStart":false})})}),makeQuery(id+"F8.opExtrude","SWEPT_FACE",FACE,{"disambiguationData":[OSD([sQuery(id+"F7.wireOp",EDGE,"E67")])]})]});}
            var Q5;
            Q5=makeQuery(id+"F8.boolean.opBoolean","INTERSECT",EDGE,{"disambiguationData":[OD(0.0)],"derivedFrom":[makeQuery(id+"F5.opExtrude","SWEPT_FACE",FACE,{"disambiguationData":[OSD([sQuery(id+"F4.wireOp",EDGE,"E30")])]}),makeQuery(id+"F8.opExtrude","SWEPT_FACE",FACE,{"disambiguationData":[OSD([sQuery(id+"F7.wireOp",EDGE,"E67")])]})]});
            fillet(context, id + "F14", {"entities" : qUnion([Q0, Q1, Q2, Q3, Q4, Q5]), "radius" : 3 * mm, "tangentPropagation" : true, "allowEdgeOverflow" : false});
        }
        {
            var Q0;
            Q0=makeQuery(id+"F1.opExtrude","CAP_EDGE",EDGE,{"disambiguationData":[OSD([sQuery(id+"F0.wireOp",EDGE,"E1.bottom")])],"isStart":false});
            fillet(context, id + "F15", {"entities" : qUnion([Q0]), "radius" : 2 * mm, "tangentPropagation" : true, "allowEdgeOverflow" : false});
        }
        {
            var Q0;
            {var subQ0=sQuery(id+"F0.wireOp",EDGE,"E21.filletArc");var subQ1=sQuery(id+"F0.wireOp",EDGE,"E7");var subQ2=sQuery(id+"F0.wireOp",EDGE,"E6");var subQ3=sQuery(id+"F0.wireOp",EDGE,"E5");var subQ4=sQuery(id+"F0.wireOp",EDGE,"E4");var subQ5=sQuery(id+"F0.wireOp",EDGE,"E22.filletArc");var subQ6=sQuery(id+"F0.wireOp",EDGE,"E1.bottom");var subQ7=sQuery(id+"F0.wireOp",EDGE,"E1.right");var subQ8=sQuery(id+"F0.wireOp",EDGE,"E1.top");var subQ9=sQuery(id+"F0.wireOp",EDGE,"E1.left");var subQ10=sQuery(id+"F0.wireOp",EDGE,"E23.filletArc");var subQ11=sQuery(id+"F0.wireOp",EDGE,"E24.filletArc");Q0=makeQuery(id+"F2.boolean.opBoolean","SPLIT",FACE,{"disambiguationData":[TD([makeQuery(id+"F1.opExtrude","SWEPT_FACE",FACE,{"disambiguationData":[OSD([subQ6])]})])],"derivedFrom":makeQuery(id+"F1.opExtrude","CAP_FACE",FACE,{"disambiguationData":[OSD([subQ6,subQ8,subQ9,subQ7,subQ4,subQ3,subQ2,subQ1,subQ0,subQ5,subQ10,subQ11])],"isStart":true})});}
            var sketch = newSketch(context, id + "F16", { "sketchPlane" : qUnion([Q0])});
            skLineSegment(sketch, "E79.0", {"start": v(-70, 90) * mm, "end": v(70, 90) * mm});
            skArc(sketch, "E79.1", {"start": v(-70, 90) * mm, "mid": v(-77.07, 87.07) * mm, "end": v(-80, 80) * mm});
            skLineSegment(sketch, "E79.2", {"start": v(-80, -80) * mm, "end": v(-80, 80) * mm});
            skArc(sketch, "E79.3", {"start": v(-80, -80) * mm, "mid": v(-77.07, -87.07) * mm, "end": v(-70, -90) * mm});
            skLineSegment(sketch, "E79.4", {"start": v(-70, -90) * mm, "end": v(70, -90) * mm});
            skArc(sketch, "E79.5", {"start": v(70, -90) * mm, "mid": v(77.07, -87.07) * mm, "end": v(80, -80) * mm});
            skLineSegment(sketch, "E79.6", {"start": v(80, -80) * mm, "end": v(80, 80) * mm});
            skArc(sketch, "E79.7", {"start": v(80, 80) * mm, "mid": v(77.07, 87.07) * mm, "end": v(70, 90) * mm});
            skArc(sketch, "E79.8", {"start": v(56.15, 48.18) * mm, "mid": v(0, 67.5) * mm, "end": v(-56.15, 48.18) * mm});
            skArc(sketch, "E79.9", {"start": v(60, 40.3) * mm, "mid": v(58.99, 44.68) * mm, "end": v(56.15, 48.18) * mm});
            skLineSegment(sketch, "E79.10", {"start": v(60, 40.3) * mm, "end": v(60, -40.3) * mm});
            skArc(sketch, "E79.11", {"start": v(56.15, -48.18) * mm, "mid": v(58.99, -44.68) * mm, "end": v(60, -40.3) * mm});
            skArc(sketch, "E79.12", {"start": v(-56.15, -48.18) * mm, "mid": v(0, -67.5) * mm, "end": v(56.15, -48.18) * mm});
            skArc(sketch, "E79.13", {"start": v(-60, -40.3) * mm, "mid": v(-58.99, -44.68) * mm, "end": v(-56.15, -48.18) * mm});
            skLineSegment(sketch, "E79.14", {"start": v(-60, 40.3) * mm, "end": v(-60, -40.3) * mm});
            skArc(sketch, "E79.15", {"start": v(-56.15, 48.18) * mm, "mid": v(-58.99, 44.68) * mm, "end": v(-60, 40.3) * mm});
            skLineSegment(sketch, "E80", {"start": v(-33, 90) * mm, "end": v(-15, 108) * mm});
            skLineSegment(sketch, "E81", {"start": v(-15, 108) * mm, "end": v(-15, 120) * mm});
            skArc(sketch, "E82", {"start": v(15, 120) * mm, "mid": v(0, 135) * mm, "end": v(-15, 120) * mm});
            skLineSegment(sketch, "E83", {"start": v(15, 120) * mm, "end": v(15, 108) * mm});
            skLineSegment(sketch, "E84", {"start": v(15, 108) * mm, "end": v(33, 90) * mm});
            skCircle(sketch, "E85", {"center": v(0, 120) * mm, "radius": 6 * mm});
            skLineSegment(sketch, "E86", {"start": v(0, 120) * mm, "end": v(0, 74.25) * mm, "construction": true});
            skLineSegment(sketch, "E87", {"start": v(-80, 0) * mm, "end": v(80, 0) * mm, "construction": true});
            skLineSegment(sketch, "E88.MirrorCS", {"start": v(15, -108) * mm, "end": v(33, -90) * mm});
            skArc(sketch, "E89.MirrorCS", {"start": v(15, -120) * mm, "mid": v(0, -135) * mm, "end": v(-15, -120) * mm});
            skLineSegment(sketch, "E90.MirrorCS", {"start": v(-33, -90) * mm, "end": v(-15, -108) * mm});
            skLineSegment(sketch, "E91.MirrorCS", {"start": v(0, -120) * mm, "end": v(0, -74.25) * mm, "construction": true});
            skCircle(sketch, "E92.MirrorC", {"center": v(0, -120) * mm, "radius": 6 * mm});
            skLineSegment(sketch, "E93.MirrorCS", {"start": v(15, -120) * mm, "end": v(15, -108) * mm});
            skLineSegment(sketch, "E94.MirrorCS", {"start": v(-15, -108) * mm, "end": v(-15, -120) * mm});
            skCircle(sketch, "E95.0", {"center": v(-60, -67.5) * mm, "radius": 4 * mm});
            skCircle(sketch, "E95.1", {"center": v(60, -67.5) * mm, "radius": 4 * mm});
            skCircle(sketch, "E95.2", {"center": v(-60, 67.5) * mm, "radius": 4 * mm});
            skCircle(sketch, "E95.3", {"center": v(60, 67.5) * mm, "radius": 4 * mm});
            skSolve(sketch);
        }
        {
            var Q0;
            Q0 = qSketchRegion(id + "F16", true);
            var Q1;
            Q1=makeQuery(id+"F2.opExtrude","CAP_FACE",FACE,{"disambiguationData":[OSD([sQuery(id+"F0.wireOp",EDGE,"E12"),sQuery(id+"F0.wireOp",EDGE,"E13"),sQuery(id+"F0.wireOp",EDGE,"E14"),sQuery(id+"F0.wireOp",EDGE,"E15"),sQuery(id+"F0.wireOp",EDGE,"E17.filletArc"),sQuery(id+"F0.wireOp",EDGE,"E18.filletArc"),sQuery(id+"F0.wireOp",EDGE,"E19.filletArc"),sQuery(id+"F0.wireOp",EDGE,"E20.filletArc"),sQuery(id+"F0.wireOp",EDGE,"E25.0"),sQuery(id+"F0.wireOp",EDGE,"E25.1"),sQuery(id+"F0.wireOp",EDGE,"E25.2"),sQuery(id+"F0.wireOp",EDGE,"E25.3"),sQuery(id+"F0.wireOp",EDGE,"E25.4"),sQuery(id+"F0.wireOp",EDGE,"E25.5"),sQuery(id+"F0.wireOp",EDGE,"E25.6"),sQuery(id+"F0.wireOp",EDGE,"E25.7")])],"isStart":false});
            extrude(context, id + "F17", {"entities" : qUnion([Q0]), "endBound" : BoundingType.UP_TO_SURFACE, "depth" : 25 * mm, "endBoundEntityFace" : qUnion([Q1]), "offsetDistance" : 25 * mm});
        }
    });
